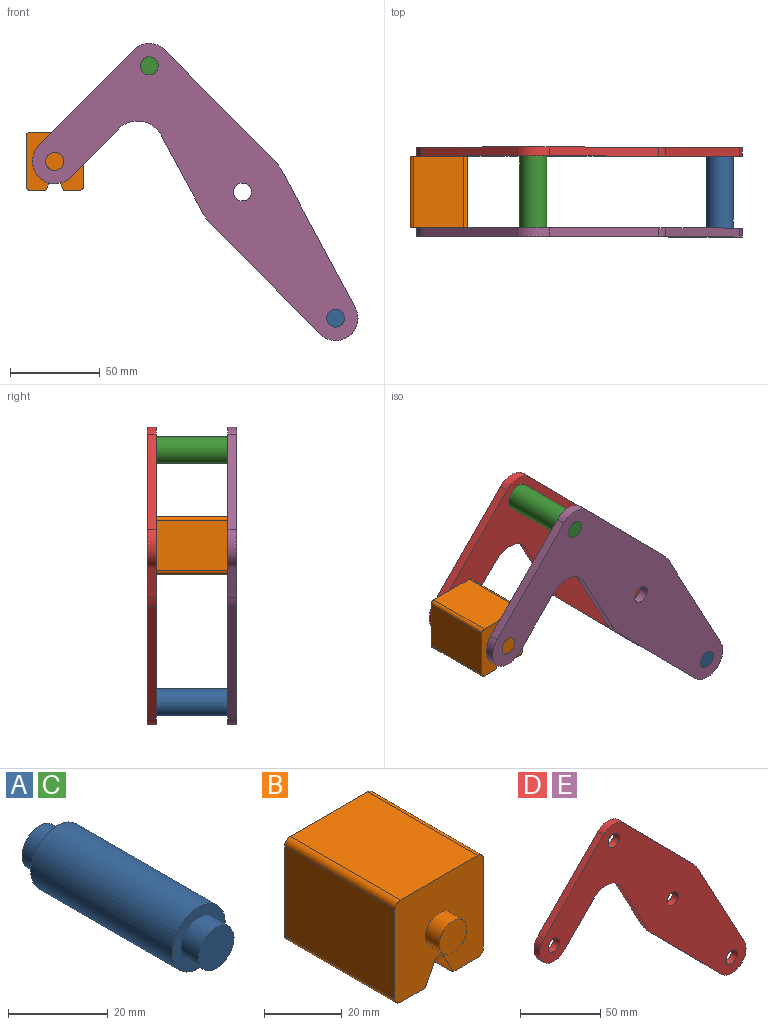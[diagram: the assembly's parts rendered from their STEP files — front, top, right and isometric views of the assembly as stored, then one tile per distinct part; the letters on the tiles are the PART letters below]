
ASSEMBLY  parts=5 mates=3
PART A: 7 faces, bbox 15x50x15 mm
  f0: cylinder r=7.5mm len=40mm, axis (0,-1,0), area 1885mm2, adj f2,f5
  f1: cylinder r=5mm len=10mm, axis (0,1,0), area 157.1mm2, adj f2,f3
  f2: plane 15x15mm, normal (0,-1,0), area 98.2mm2, adj f0,f1
  f3: plane 10x10mm, normal (0,-1,0), area 78.5mm2, adj f1
  f4: cylinder r=5mm len=10mm, axis (0,-1,0), area 157.1mm2, adj f5,f6
  f5: plane 15x15mm, normal (0,1,0), area 98.2mm2, adj f0,f4
  f6: plane 10x10mm, normal (0,1,0), area 78.5mm2, adj f4
PART B: 18 faces, bbox 32.1x50x32.1 mm
  f0: plane 40x28.08mm, normal (1,0,0), area 1123.1mm2, adj f4,f10,f13,f14
  f1: plane 40x9.04mm, normal (0,0,-1), area 361.6mm2, adj f2,f4,f10,f14
  f2: plane 40x6.42mm, normal (-0.89,0,-0.45), area 287.2mm2, adj f1,f4,f10,f15
  f3: plane 40x6.42mm, normal (0.89,0,-0.45), area 287.2mm2, adj f4,f5,f10,f15
  f4: plane 32.08x32.08mm, normal (0,-1,0), area 900.6mm2, adj f0,f1,f2,f3,f5,f6,f7,f9
  f5: plane 40x9.04mm, normal (0,0,-1), area 361.6mm2, adj f3,f4,f10,f16
  f6: plane 40x28.08mm, normal (0,0,1), area 1123.1mm2, adj f4,f10,f13,f17
  f7: plane 40x28.08mm, normal (-1,0,0), area 1123.1mm2, adj f4,f10,f16,f17
  f8: plane 10x10mm, normal (0,-1,0), area 78.5mm2, adj f9
  f9: cylinder r=5mm len=10mm, axis (0,1,0), area 157.1mm2, adj f4,f8
  f10: plane 32.08x32.08mm, normal (0,1,0), area 900.6mm2, adj f0,f1,f2,f3,f5,f6,f7,f12
  f11: plane 10x10mm, normal (0,1,0), area 78.5mm2, adj f12
  f12: cylinder r=5mm len=10mm, axis (0,-1,0), area 157.1mm2, adj f10,f11
  f13: cylinder r=2mm len=40mm, axis (0,1,0), area 125.7mm2, adj f0,f4,f6,f10
  f14: cylinder r=2mm len=40mm, axis (0,-1,0), area 125.7mm2, adj f0,f1,f4,f10
  f15: cylinder r=2mm len=40mm, axis (0,1,0), area 177.1mm2, adj f2,f3,f4,f10
  f16: cylinder r=2mm len=40mm, axis (0,1,0), area 125.7mm2, adj f4,f5,f7,f10
  f17: cylinder r=2mm len=40mm, axis (0,-1,0), area 125.7mm2, adj f4,f6,f7,f10
PART C: same geometry as A
PART D: 18 faces, bbox 181.7x5x165.8 mm
  f0: plane 43.49x23.35mm, normal (-0.88,0,-0.47), area 246.8mm2, adj f1,f14,f16,f17
  f1: cylinder r=25mm len=5.75mm, axis (0,1,0), area 35.8mm2, adj f0,f2,f16,f17
  f2: plane 61.6x60.87mm, normal (-0.71,0,-0.7), area 433mm2, adj f1,f3,f16,f17
  f3: cylinder r=12.5mm len=21.39mm, axis (0,1,0), area 178.4mm2, adj f2,f4,f16,f17
  f4: plane 76.3x40.96mm, normal (0.88,0,0.47), area 433mm2, adj f3,f5,f16,f17
  f5: cylinder r=25mm len=5.75mm, axis (0,1,0), area 35.8mm2, adj f4,f6,f16,f17
  f6: plane 61.6x60.87mm, normal (0.71,0,0.7), area 433mm2, adj f5,f7,f16,f17
  f7: cylinder r=12.5mm len=17.78mm, axis (0,1,0), area 98.9mm2, adj f6,f8,f16,f17
  f8: plane 53.35x52.71mm, normal (-0.71,0,0.7), area 375mm2, adj f7,f9,f16,f17
  f9: cylinder r=12.5mm len=21.39mm, axis (0,1,0), area 196.3mm2, adj f8,f10,f16,f17
  f10: plane 26.86x26.54mm, normal (0.71,0,-0.7), area 188.8mm2, adj f9,f14,f16,f17
  f11: cylinder r=5mm len=10mm, axis (0,1,0), area 157.1mm2, adj f16,f17
  f12: cylinder r=5mm len=10mm, axis (0,1,0), area 157.1mm2, adj f16,f17
  f13: cylinder r=5mm len=10mm, axis (0,1,0), area 157.1mm2, adj f16,f17
  f14: cylinder r=15mm len=23.89mm, axis (0,1,0), area 140.2mm2, adj f0,f10,f16,f17
  f15: cylinder r=5mm len=10mm, axis (0,1,0), area 157.1mm2, adj f16,f17
  f16: plane 181.66x165.78mm, normal (0,-1,0), area 8710.1mm2, adj f0,f1,f2,f3,f4,f5,f6,f7
  f17: plane 181.66x165.78mm, normal (0,1,0), area 8710.1mm2, adj f0,f1,f2,f3,f4,f5,f6,f7
PART E: same geometry as D
PLACE A t=(103.95,-20,-140.78)mm
PLACE B t=(0,-20,0)mm
PLACE C t=(0,-20,0)mm
PLACE D t=(0,25,0)mm
PLACE E t=(0,-20,0)mm fixed
MATE fastened C.f0 <-> D.f7  axis (0,1,0) through (-51.98,20,70.39)mm
MATE revolute B.f9 <-> E.f9  axis (0,-1,0) through (-104.69,-20,17.04)mm
MATE fastened A.f0 <-> D.f3  axis (0,1,0) through (51.98,20,-70.39)mm
